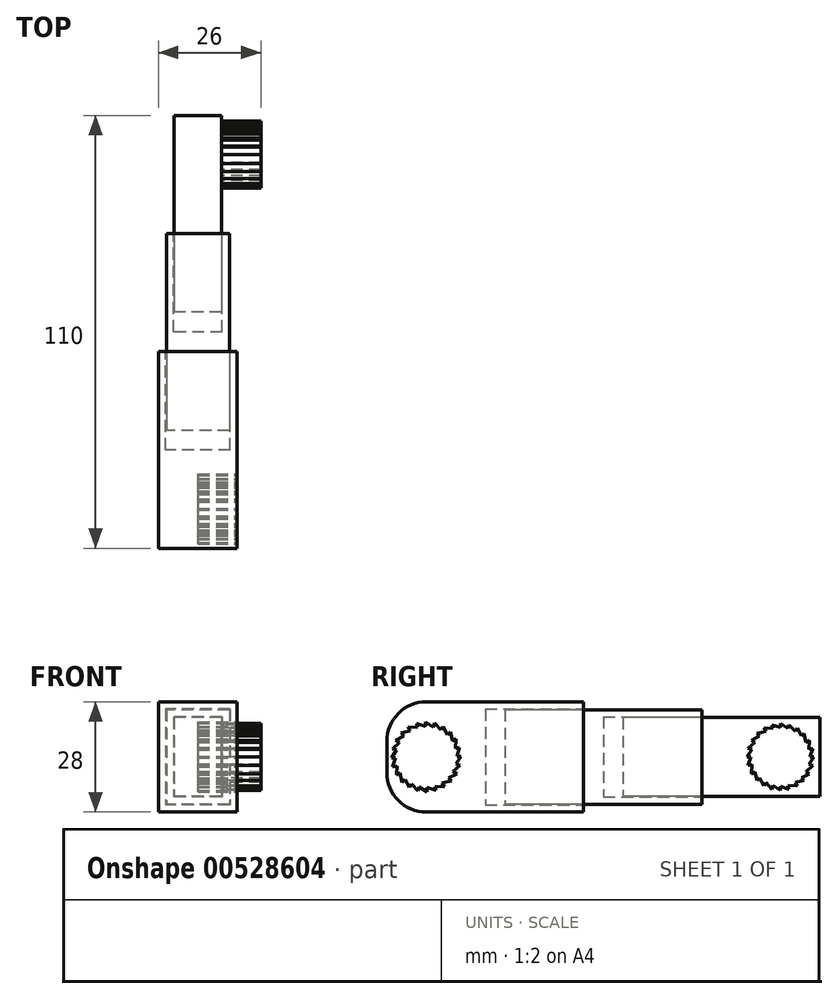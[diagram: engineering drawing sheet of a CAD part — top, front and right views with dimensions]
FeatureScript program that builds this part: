
annotation { "Feature Type Name" : "Feature", "Feature Type Description" : "" }
export const myFeature = defineFeature(function(context is Context, id is Id, definition is map)
    precondition{}
    {
        {
            var Q0;
            Q0=qCreatedBy(makeId("Right.planeOp"),FACE);
            var sketch = newSketch(context, id + "F0", { "sketchPlane" : qUnion([Q0])});
            skLineSegment(sketch, "E0.bottom", {"start": v(50, 0) * mm, "end": v(0, 0) * mm});
            skLineSegment(sketch, "E0.top", {"start": v(50, 28) * mm, "end": v(0, 28) * mm});
            skLineSegment(sketch, "E0.left", {"start": v(50, 0) * mm, "end": v(50, 28) * mm});
            skLineSegment(sketch, "E0.right", {"start": v(0, 0) * mm, "end": v(0, 28) * mm});
            skSolve(sketch);
        }
        {
            var Q0;
            Q0=makeQuery(id+"F0.imprint","IMPRINT",FACE,{"disambiguationData":[TD([[makeQuery(id+"F0.imprint","IMPRINT",EDGE,{"derivedFrom":sQuery(id+"F0.wireOp",EDGE,"E0.bottom")}),-1.0]])]});
            extrude(context, id + "F1", {"entities" : qUnion([Q0]), "depth" : 20 * mm, "offsetDistance" : 25 * mm});
        }
        {
            var Q0;
            Q0=makeQuery(id+"F1.opExtrude","CAP_FACE",FACE,{"disambiguationData":[OSD([sQuery(id+"F0.wireOp",EDGE,"E0.bottom"),sQuery(id+"F0.wireOp",EDGE,"E0.top"),sQuery(id+"F0.wireOp",EDGE,"E0.left"),sQuery(id+"F0.wireOp",EDGE,"E0.right")])],"isStart":false});
            var sketch = newSketch(context, id + "F2", { "sketchPlane" : qUnion([Q0])});
            skCircle(sketch, "E1", {"center": v(10, 14) * mm, "radius": 7.5 * mm});
            skLineSegment(sketch, "E2", {"start": v(10, 21.5) * mm, "end": v(10, 22.5) * mm});
            skPoint(sketch, "E3.center", {"position": v(5.72, 10.17) * mm});
            skLineSegment(sketch, "E4", {"start": v(10, 22.5) * mm, "end": v(11.94, 21.24) * mm});
            skLineSegment(sketch, "E5.1.0", {"start": v(12.2, 22.21) * mm, "end": v(13.75, 20.5) * mm});
            skLineSegment(sketch, "E5.1.1", {"start": v(11.94, 21.24) * mm, "end": v(12.2, 22.21) * mm});
            skLineSegment(sketch, "E5.2.0", {"start": v(14.25, 21.36) * mm, "end": v(15.3, 19.3) * mm});
            skLineSegment(sketch, "E5.2.1", {"start": v(13.75, 20.5) * mm, "end": v(14.25, 21.36) * mm});
            skLineSegment(sketch, "E5.3.0", {"start": v(16.01, 20.01) * mm, "end": v(16.5, 17.75) * mm});
            skLineSegment(sketch, "E5.3.1", {"start": v(15.3, 19.3) * mm, "end": v(16.01, 20.01) * mm});
            skLineSegment(sketch, "E5.4.0", {"start": v(17.36, 18.25) * mm, "end": v(17.24, 15.94) * mm});
            skLineSegment(sketch, "E5.4.1", {"start": v(16.5, 17.75) * mm, "end": v(17.36, 18.25) * mm});
            skLineSegment(sketch, "E5.5.0", {"start": v(18.21, 16.2) * mm, "end": v(17.5, 14) * mm});
            skLineSegment(sketch, "E5.5.1", {"start": v(17.24, 15.94) * mm, "end": v(18.21, 16.2) * mm});
            skLineSegment(sketch, "E5.6.0", {"start": v(18.5, 14) * mm, "end": v(17.24, 12.06) * mm});
            skLineSegment(sketch, "E5.6.1", {"start": v(17.5, 14) * mm, "end": v(18.5, 14) * mm});
            skLineSegment(sketch, "E5.7.0", {"start": v(18.21, 11.8) * mm, "end": v(16.5, 10.25) * mm});
            skLineSegment(sketch, "E5.7.1", {"start": v(17.24, 12.06) * mm, "end": v(18.21, 11.8) * mm});
            skLineSegment(sketch, "E5.8.0", {"start": v(17.36, 9.75) * mm, "end": v(15.3, 8.7) * mm});
            skLineSegment(sketch, "E5.8.1", {"start": v(16.5, 10.25) * mm, "end": v(17.36, 9.75) * mm});
            skLineSegment(sketch, "E5.9.0", {"start": v(16.01, 7.99) * mm, "end": v(13.75, 7.5) * mm});
            skLineSegment(sketch, "E5.9.1", {"start": v(15.3, 8.7) * mm, "end": v(16.01, 7.99) * mm});
            skLineSegment(sketch, "E5.10.0", {"start": v(14.25, 6.64) * mm, "end": v(11.94, 6.76) * mm});
            skLineSegment(sketch, "E5.10.1", {"start": v(13.75, 7.5) * mm, "end": v(14.25, 6.64) * mm});
            skLineSegment(sketch, "E5.11.0", {"start": v(12.2, 5.79) * mm, "end": v(10, 6.5) * mm});
            skLineSegment(sketch, "E5.11.1", {"start": v(11.94, 6.76) * mm, "end": v(12.2, 5.79) * mm});
            skLineSegment(sketch, "E5.12.0", {"start": v(10, 5.5) * mm, "end": v(8.06, 6.76) * mm});
            skLineSegment(sketch, "E5.12.1", {"start": v(10, 6.5) * mm, "end": v(10, 5.5) * mm});
            skLineSegment(sketch, "E5.13.0", {"start": v(7.8, 5.79) * mm, "end": v(6.25, 7.5) * mm});
            skLineSegment(sketch, "E5.13.1", {"start": v(8.06, 6.76) * mm, "end": v(7.8, 5.79) * mm});
            skLineSegment(sketch, "E5.14.0", {"start": v(5.75, 6.64) * mm, "end": v(4.7, 8.7) * mm});
            skLineSegment(sketch, "E5.14.1", {"start": v(6.25, 7.5) * mm, "end": v(5.75, 6.64) * mm});
            skLineSegment(sketch, "E5.15.0", {"start": v(3.99, 7.99) * mm, "end": v(3.5, 10.25) * mm});
            skLineSegment(sketch, "E5.15.1", {"start": v(4.7, 8.7) * mm, "end": v(3.99, 7.99) * mm});
            skLineSegment(sketch, "E5.16.0", {"start": v(2.64, 9.75) * mm, "end": v(2.76, 12.06) * mm});
            skLineSegment(sketch, "E5.16.1", {"start": v(3.5, 10.25) * mm, "end": v(2.64, 9.75) * mm});
            skLineSegment(sketch, "E5.17.0", {"start": v(1.79, 11.8) * mm, "end": v(2.5, 14) * mm});
            skLineSegment(sketch, "E5.17.1", {"start": v(2.76, 12.06) * mm, "end": v(1.79, 11.8) * mm});
            skLineSegment(sketch, "E5.18.0", {"start": v(1.5, 14) * mm, "end": v(2.76, 15.94) * mm});
            skLineSegment(sketch, "E5.18.1", {"start": v(2.5, 14) * mm, "end": v(1.5, 14) * mm});
            skLineSegment(sketch, "E5.19.0", {"start": v(1.79, 16.2) * mm, "end": v(3.5, 17.75) * mm});
            skLineSegment(sketch, "E5.19.1", {"start": v(2.76, 15.94) * mm, "end": v(1.79, 16.2) * mm});
            skLineSegment(sketch, "E5.20.0", {"start": v(2.64, 18.25) * mm, "end": v(4.7, 19.3) * mm});
            skLineSegment(sketch, "E5.20.1", {"start": v(3.5, 17.75) * mm, "end": v(2.64, 18.25) * mm});
            skLineSegment(sketch, "E5.21.0", {"start": v(3.99, 20.01) * mm, "end": v(6.25, 20.5) * mm});
            skLineSegment(sketch, "E5.21.1", {"start": v(4.7, 19.3) * mm, "end": v(3.99, 20.01) * mm});
            skLineSegment(sketch, "E5.22.0", {"start": v(5.75, 21.36) * mm, "end": v(8.06, 21.24) * mm});
            skLineSegment(sketch, "E5.22.1", {"start": v(6.25, 20.5) * mm, "end": v(5.75, 21.36) * mm});
            skLineSegment(sketch, "E5.anchor1", {"start": v(10, 14) * mm, "end": v(10, 21.5) * mm, "construction": true});
            skLineSegment(sketch, "E5.anchor2", {"start": v(10, 14) * mm, "end": v(8.06, 21.24) * mm, "construction": true});
            skLineSegment(sketch, "E6.3.23.0", {"start": v(8.06, 21.24) * mm, "end": v(7.8, 22.21) * mm});
            skLineSegment(sketch, "E6.4.23.0", {"start": v(7.8, 22.21) * mm, "end": v(10, 21.5) * mm});
            skLineSegment(sketch, "E7.0", {"start": v(18.51, 16.49) * mm, "end": v(17.77, 14.2) * mm});
            skLineSegment(sketch, "E7.1", {"start": v(17.46, 16.2) * mm, "end": v(18.51, 16.49) * mm});
            skLineSegment(sketch, "E7.2", {"start": v(2.42, 9.4) * mm, "end": v(2.54, 11.8) * mm});
            skLineSegment(sketch, "E7.3", {"start": v(3.37, 9.94) * mm, "end": v(2.42, 9.4) * mm});
            skLineSegment(sketch, "E7.4", {"start": v(3.87, 7.59) * mm, "end": v(3.37, 9.94) * mm});
            skLineSegment(sketch, "E7.5", {"start": v(4.64, 8.36) * mm, "end": v(3.87, 7.59) * mm});
            skLineSegment(sketch, "E7.6", {"start": v(5.74, 6.22) * mm, "end": v(4.64, 8.36) * mm});
            skLineSegment(sketch, "E7.7", {"start": v(6.29, 7.17) * mm, "end": v(5.74, 6.22) * mm});
            skLineSegment(sketch, "E7.8", {"start": v(7.9, 5.38) * mm, "end": v(6.29, 7.17) * mm});
            skLineSegment(sketch, "E7.9", {"start": v(8.18, 6.44) * mm, "end": v(7.9, 5.38) * mm});
            skLineSegment(sketch, "E7.10", {"start": v(10.2, 5.13) * mm, "end": v(8.18, 6.44) * mm});
            skLineSegment(sketch, "E7.11", {"start": v(10.2, 6.23) * mm, "end": v(10.2, 5.13) * mm});
            skLineSegment(sketch, "E7.12", {"start": v(12.49, 5.49) * mm, "end": v(10.2, 6.23) * mm});
            skLineSegment(sketch, "E7.13", {"start": v(12.2, 6.54) * mm, "end": v(12.49, 5.49) * mm});
            skLineSegment(sketch, "E7.14", {"start": v(18.62, 11.9) * mm, "end": v(16.83, 10.29) * mm});
            skLineSegment(sketch, "E7.15", {"start": v(17.56, 12.18) * mm, "end": v(18.62, 11.9) * mm});
            skLineSegment(sketch, "E7.16", {"start": v(18.87, 14.2) * mm, "end": v(17.56, 12.18) * mm});
            skLineSegment(sketch, "E7.17", {"start": v(17.77, 14.2) * mm, "end": v(18.87, 14.2) * mm});
            skLineSegment(sketch, "E7.18", {"start": v(16.83, 10.29) * mm, "end": v(17.78, 9.74) * mm});
            skLineSegment(sketch, "E7.19", {"start": v(17.78, 9.74) * mm, "end": v(15.64, 8.64) * mm});
            skLineSegment(sketch, "E7.20", {"start": v(15.64, 8.64) * mm, "end": v(16.41, 7.87) * mm});
            skLineSegment(sketch, "E7.21", {"start": v(16.41, 7.87) * mm, "end": v(14.06, 7.37) * mm});
            skLineSegment(sketch, "E7.22", {"start": v(14.06, 7.37) * mm, "end": v(14.6, 6.42) * mm});
            skLineSegment(sketch, "E7.23", {"start": v(14.6, 6.42) * mm, "end": v(12.2, 6.54) * mm});
            skLineSegment(sketch, "E7.24", {"start": v(2.54, 11.8) * mm, "end": v(1.49, 11.51) * mm});
            skLineSegment(sketch, "E7.25", {"start": v(1.49, 11.51) * mm, "end": v(2.23, 13.8) * mm});
            skLineSegment(sketch, "E7.26", {"start": v(2.23, 13.8) * mm, "end": v(1.13, 13.8) * mm});
            skLineSegment(sketch, "E7.27", {"start": v(1.13, 13.8) * mm, "end": v(2.44, 15.82) * mm});
            skLineSegment(sketch, "E7.28", {"start": v(2.44, 15.82) * mm, "end": v(1.38, 16.1) * mm});
            skLineSegment(sketch, "E7.29", {"start": v(1.38, 16.1) * mm, "end": v(3.17, 17.71) * mm});
            skLineSegment(sketch, "E7.30", {"start": v(3.17, 17.71) * mm, "end": v(2.22, 18.26) * mm});
            skLineSegment(sketch, "E7.31", {"start": v(2.22, 18.26) * mm, "end": v(4.36, 19.36) * mm});
            skLineSegment(sketch, "E7.32", {"start": v(4.36, 19.36) * mm, "end": v(3.59, 20.13) * mm});
            skLineSegment(sketch, "E7.33", {"start": v(3.59, 20.13) * mm, "end": v(5.94, 20.63) * mm});
            skLineSegment(sketch, "E7.34", {"start": v(5.94, 20.63) * mm, "end": v(5.4, 21.58) * mm});
            skLineSegment(sketch, "E7.35", {"start": v(5.4, 21.58) * mm, "end": v(7.8, 21.46) * mm});
            skLineSegment(sketch, "E7.36", {"start": v(7.8, 21.46) * mm, "end": v(7.51, 22.51) * mm});
            skLineSegment(sketch, "E7.37", {"start": v(7.51, 22.51) * mm, "end": v(9.8, 21.77) * mm});
            skLineSegment(sketch, "E7.38", {"start": v(9.8, 21.77) * mm, "end": v(9.8, 22.87) * mm});
            skLineSegment(sketch, "E7.39", {"start": v(9.8, 22.87) * mm, "end": v(11.82, 21.56) * mm});
            skLineSegment(sketch, "E7.40", {"start": v(11.82, 21.56) * mm, "end": v(12.1, 22.62) * mm});
            skLineSegment(sketch, "E7.41", {"start": v(12.1, 22.62) * mm, "end": v(13.71, 20.83) * mm});
            skLineSegment(sketch, "E7.42", {"start": v(13.71, 20.83) * mm, "end": v(14.26, 21.78) * mm});
            skLineSegment(sketch, "E7.43", {"start": v(14.26, 21.78) * mm, "end": v(15.36, 19.64) * mm});
            skLineSegment(sketch, "E7.44", {"start": v(15.36, 19.64) * mm, "end": v(16.13, 20.41) * mm});
            skLineSegment(sketch, "E7.45", {"start": v(16.13, 20.41) * mm, "end": v(16.63, 18.06) * mm});
            skLineSegment(sketch, "E7.46", {"start": v(16.63, 18.06) * mm, "end": v(17.58, 18.6) * mm});
            skLineSegment(sketch, "E7.47", {"start": v(17.58, 18.6) * mm, "end": v(17.46, 16.2) * mm});
            skSolve(sketch);
        }
        {
            var Q0;
            {var subQ0=sQuery(id+"F2.wireOp",EDGE,"E1");var subQ17=makeQuery(id+"F2.imprint","INTERSECT",VERTEX,{"derivedFrom":[subQ0,sQuery(id+"F2.wireOp",EDGE,"E5.4.0"),sQuery(id+"F2.wireOp",EDGE,"E5.5.1")]});Q0=makeQuery(id+"F2.imprint","IMPRINT",FACE,{"disambiguationData":[TD([[makeQuery(id+"F2.imprint","IMPRINT",EDGE,{"disambiguationData":[TD([[subQ17,1.0]])],"derivedFrom":subQ0}),1.0]])]});}
            var Q1;
            {var subQ2=sQuery(id+"F2.wireOp",EDGE,"E6.3.23.0");Q1=makeQuery(id+"F2.imprint","IMPRINT",FACE,{"disambiguationData":[TD([[makeQuery(id+"F2.imprint","IMPRINT",EDGE,{"derivedFrom":subQ2}),-1.0]])]});}
            var Q2;
            {var subQ2=sQuery(id+"F2.wireOp",EDGE,"E5.22.0");Q2=makeQuery(id+"F2.imprint","IMPRINT",FACE,{"disambiguationData":[TD([[makeQuery(id+"F2.imprint","IMPRINT",EDGE,{"derivedFrom":subQ2}),-1.0]])]});}
            var Q3;
            {var subQ2=sQuery(id+"F2.wireOp",EDGE,"E5.21.0");Q3=makeQuery(id+"F2.imprint","IMPRINT",FACE,{"disambiguationData":[TD([[makeQuery(id+"F2.imprint","IMPRINT",EDGE,{"derivedFrom":subQ2}),-1.0]])]});}
            var Q4;
            {var subQ2=sQuery(id+"F2.wireOp",EDGE,"E5.20.0");Q4=makeQuery(id+"F2.imprint","IMPRINT",FACE,{"disambiguationData":[TD([[makeQuery(id+"F2.imprint","IMPRINT",EDGE,{"derivedFrom":subQ2}),-1.0]])]});}
            var Q5;
            {var subQ2=sQuery(id+"F2.wireOp",EDGE,"E5.19.0");Q5=makeQuery(id+"F2.imprint","IMPRINT",FACE,{"disambiguationData":[TD([[makeQuery(id+"F2.imprint","IMPRINT",EDGE,{"derivedFrom":subQ2}),-1.0]])]});}
            var Q6;
            {var subQ2=sQuery(id+"F2.wireOp",EDGE,"E5.17.0");Q6=makeQuery(id+"F2.imprint","IMPRINT",FACE,{"disambiguationData":[TD([[makeQuery(id+"F2.imprint","IMPRINT",EDGE,{"derivedFrom":subQ2}),-1.0]])]});}
            var Q7;
            {var subQ2=sQuery(id+"F2.wireOp",EDGE,"E5.18.0");Q7=makeQuery(id+"F2.imprint","IMPRINT",FACE,{"disambiguationData":[TD([[makeQuery(id+"F2.imprint","IMPRINT",EDGE,{"derivedFrom":subQ2}),-1.0]])]});}
            var Q8;
            {var subQ2=sQuery(id+"F2.wireOp",EDGE,"E5.16.0");Q8=makeQuery(id+"F2.imprint","IMPRINT",FACE,{"disambiguationData":[TD([[makeQuery(id+"F2.imprint","IMPRINT",EDGE,{"derivedFrom":subQ2}),-1.0]])]});}
            var Q9;
            {var subQ0=sQuery(id+"F2.wireOp",EDGE,"E2");Q9=makeQuery(id+"F2.imprint","IMPRINT",FACE,{"disambiguationData":[TD([[makeQuery(id+"F2.imprint","IMPRINT",EDGE,{"derivedFrom":subQ0}),-1.0]])]});}
            var Q10;
            {var subQ2=sQuery(id+"F2.wireOp",EDGE,"E5.1.0");Q10=makeQuery(id+"F2.imprint","IMPRINT",FACE,{"disambiguationData":[TD([[makeQuery(id+"F2.imprint","IMPRINT",EDGE,{"derivedFrom":subQ2}),-1.0]])]});}
            var Q11;
            {var subQ2=sQuery(id+"F2.wireOp",EDGE,"E5.2.0");Q11=makeQuery(id+"F2.imprint","IMPRINT",FACE,{"disambiguationData":[TD([[makeQuery(id+"F2.imprint","IMPRINT",EDGE,{"derivedFrom":subQ2}),-1.0]])]});}
            var Q12;
            {var subQ2=sQuery(id+"F2.wireOp",EDGE,"E5.3.0");Q12=makeQuery(id+"F2.imprint","IMPRINT",FACE,{"disambiguationData":[TD([[makeQuery(id+"F2.imprint","IMPRINT",EDGE,{"derivedFrom":subQ2}),-1.0]])]});}
            var Q13;
            {var subQ2=sQuery(id+"F2.wireOp",EDGE,"E5.4.0");Q13=makeQuery(id+"F2.imprint","IMPRINT",FACE,{"disambiguationData":[TD([[makeQuery(id+"F2.imprint","IMPRINT",EDGE,{"derivedFrom":subQ2}),-1.0]])]});}
            var Q14;
            {var subQ2=sQuery(id+"F2.wireOp",EDGE,"E5.5.0");Q14=makeQuery(id+"F2.imprint","IMPRINT",FACE,{"disambiguationData":[TD([[makeQuery(id+"F2.imprint","IMPRINT",EDGE,{"derivedFrom":subQ2}),-1.0]])]});}
            var Q15;
            {var subQ2=sQuery(id+"F2.wireOp",EDGE,"E5.6.0");Q15=makeQuery(id+"F2.imprint","IMPRINT",FACE,{"disambiguationData":[TD([[makeQuery(id+"F2.imprint","IMPRINT",EDGE,{"derivedFrom":subQ2}),-1.0]])]});}
            var Q16;
            {var subQ2=sQuery(id+"F2.wireOp",EDGE,"E5.7.0");Q16=makeQuery(id+"F2.imprint","IMPRINT",FACE,{"disambiguationData":[TD([[makeQuery(id+"F2.imprint","IMPRINT",EDGE,{"derivedFrom":subQ2}),-1.0]])]});}
            var Q17;
            {var subQ2=sQuery(id+"F2.wireOp",EDGE,"E5.8.0");Q17=makeQuery(id+"F2.imprint","IMPRINT",FACE,{"disambiguationData":[TD([[makeQuery(id+"F2.imprint","IMPRINT",EDGE,{"derivedFrom":subQ2}),-1.0]])]});}
            var Q18;
            {var subQ2=sQuery(id+"F2.wireOp",EDGE,"E5.9.0");Q18=makeQuery(id+"F2.imprint","IMPRINT",FACE,{"disambiguationData":[TD([[makeQuery(id+"F2.imprint","IMPRINT",EDGE,{"derivedFrom":subQ2}),-1.0]])]});}
            var Q19;
            {var subQ2=sQuery(id+"F2.wireOp",EDGE,"E5.10.0");Q19=makeQuery(id+"F2.imprint","IMPRINT",FACE,{"disambiguationData":[TD([[makeQuery(id+"F2.imprint","IMPRINT",EDGE,{"derivedFrom":subQ2}),-1.0]])]});}
            var Q20;
            {var subQ2=sQuery(id+"F2.wireOp",EDGE,"E5.11.0");Q20=makeQuery(id+"F2.imprint","IMPRINT",FACE,{"disambiguationData":[TD([[makeQuery(id+"F2.imprint","IMPRINT",EDGE,{"derivedFrom":subQ2}),-1.0]])]});}
            var Q21;
            {var subQ2=sQuery(id+"F2.wireOp",EDGE,"E5.12.0");Q21=makeQuery(id+"F2.imprint","IMPRINT",FACE,{"disambiguationData":[TD([[makeQuery(id+"F2.imprint","IMPRINT",EDGE,{"derivedFrom":subQ2}),-1.0]])]});}
            var Q22;
            {var subQ2=sQuery(id+"F2.wireOp",EDGE,"E5.13.0");Q22=makeQuery(id+"F2.imprint","IMPRINT",FACE,{"disambiguationData":[TD([[makeQuery(id+"F2.imprint","IMPRINT",EDGE,{"derivedFrom":subQ2}),-1.0]])]});}
            var Q23;
            {var subQ2=sQuery(id+"F2.wireOp",EDGE,"E5.14.0");Q23=makeQuery(id+"F2.imprint","IMPRINT",FACE,{"disambiguationData":[TD([[makeQuery(id+"F2.imprint","IMPRINT",EDGE,{"derivedFrom":subQ2}),-1.0]])]});}
            var Q24;
            {var subQ2=sQuery(id+"F2.wireOp",EDGE,"E5.15.0");Q24=makeQuery(id+"F2.imprint","IMPRINT",FACE,{"disambiguationData":[TD([[makeQuery(id+"F2.imprint","IMPRINT",EDGE,{"derivedFrom":subQ2}),-1.0]])]});}
            var Q25;
            Q25=makeQuery(id+"F2.imprint","IMPRINT",FACE,{"disambiguationData":[TD([[makeQuery(id+"F2.imprint","IMPRINT",EDGE,{"derivedFrom":sQuery(id+"F2.wireOp",EDGE,"E2")}),1.0]])]});
            extrude(context, id + "F3", {"entities" : qUnion([Q0, Q1, Q2, Q3, Q4, Q5, Q6, Q7, Q8, Q9, Q10, Q11, Q12, Q13, Q14, Q15, Q16, Q17, Q18, Q19, Q20, Q21, Q22, Q23, Q24, Q25]), "operationType" : NewBodyOperationType.REMOVE, "oppositeDirection" : true, "depth" : 10 * mm, "offsetDistance" : 25 * mm});
        }
        {
            var Q0;
            Q0=makeQuery(id+"F1.opExtrude","SWEPT_EDGE",EDGE,{"disambiguationData":[OSD([sQuery(id+"F0.wireOp",EDGE,"E0.bottom"),sQuery(id+"F0.wireOp",EDGE,"E0.right")])]});
            var Q1;
            Q1=makeQuery(id+"F1.opExtrude","SWEPT_EDGE",EDGE,{"disambiguationData":[OSD([sQuery(id+"F0.wireOp",EDGE,"E0.top"),sQuery(id+"F0.wireOp",EDGE,"E0.right")])]});
            fillet(context, id + "F4", {"entities" : qUnion([Q0, Q1]), "radius" : 10 * mm, "tangentPropagation" : true, "allowEdgeOverflow" : false});
        }
        {
            var Q0;
            Q0=makeQuery(id+"F1.opExtrude","SWEPT_FACE",FACE,{"disambiguationData":[OSD([sQuery(id+"F0.wireOp",EDGE,"E0.left")])]});
            var sketch = newSketch(context, id + "F5", { "sketchPlane" : qUnion([Q0])});
            skLineSegment(sketch, "E8", {"start": v(-20, 28) * mm, "end": v(0, 0) * mm, "construction": true});
            skLineSegment(sketch, "E9", {"start": v(0, 28) * mm, "end": v(-20, 0) * mm, "construction": true});
            skLineSegment(sketch, "E10.bottom", {"start": v(-18, 26) * mm, "end": v(-2, 26) * mm});
            skLineSegment(sketch, "E10.top", {"start": v(-18, 2) * mm, "end": v(-2, 2) * mm});
            skLineSegment(sketch, "E10.left", {"start": v(-18, 26) * mm, "end": v(-18, 2) * mm});
            skLineSegment(sketch, "E10.right", {"start": v(-2, 26) * mm, "end": v(-2, 2) * mm});
            skPoint(sketch, "E10.middle", {"position": v(-10, 14) * mm});
            skLineSegment(sketch, "E11.0", {"start": v(-18.2, 26.2) * mm, "end": v(-1.8, 26.2) * mm});
            skLineSegment(sketch, "E11.1", {"start": v(-18.2, 26.2) * mm, "end": v(-18.2, 1.8) * mm});
            skLineSegment(sketch, "E11.2", {"start": v(-18.2, 1.8) * mm, "end": v(-1.8, 1.8) * mm});
            skLineSegment(sketch, "E11.3", {"start": v(-1.8, 26.2) * mm, "end": v(-1.8, 1.8) * mm});
            skSolve(sketch);
        }
        {
            var Q0;
            Q0=makeQuery(id+"F5.imprint","IMPRINT",FACE,{"disambiguationData":[TD([[makeQuery(id+"F5.imprint","IMPRINT",EDGE,{"derivedFrom":sQuery(id+"F5.wireOp",EDGE,"E10.bottom")}),-1.0]])]});
            var Q1;
            Q1=makeQuery(id+"F5.imprint","IMPRINT",FACE,{"disambiguationData":[TD([[makeQuery(id+"F5.imprint","IMPRINT",EDGE,{"derivedFrom":sQuery(id+"F5.wireOp",EDGE,"E10.bottom")}),1.0]])]});
            extrude(context, id + "F6", {"entities" : qUnion([Q0, Q1]), "operationType" : NewBodyOperationType.REMOVE, "oppositeDirection" : true, "depth" : 25 * mm, "offsetDistance" : 25 * mm});
        }
        {
            var Q0;
            Q0=makeQuery(id+"F5.imprint","IMPRINT",FACE,{"disambiguationData":[TD([[makeQuery(id+"F5.imprint","IMPRINT",EDGE,{"derivedFrom":sQuery(id+"F5.wireOp",EDGE,"E10.bottom")}),-1.0]])]});
            extrude(context, id + "F7", {"entities" : qUnion([Q0]), "depth" : 30 * mm, "offsetDistance" : 25 * mm, "hasSecondDirection" : true, "secondDirectionOppositeDirection" : true, "secondDirectionDepth" : 20 * mm});
        }
        {
            var Q0;
            Q0=makeQuery(id+"F7.opExtrude","CAP_FACE",FACE,{"disambiguationData":[OSD([sQuery(id+"F5.wireOp",EDGE,"E10.bottom"),sQuery(id+"F5.wireOp",EDGE,"E10.top"),sQuery(id+"F5.wireOp",EDGE,"E10.left"),sQuery(id+"F5.wireOp",EDGE,"E10.right")])],"isStart":false});
            var sketch = newSketch(context, id + "F8", { "sketchPlane" : qUnion([Q0])});
            skLineSegment(sketch, "E12", {"start": v(-18, 2) * mm, "end": v(-2, 26) * mm, "construction": true});
            skLineSegment(sketch, "E13", {"start": v(-18, 26) * mm, "end": v(-2, 2) * mm, "construction": true});
            skLineSegment(sketch, "E14.bottom", {"start": v(-16, 24) * mm, "end": v(-4, 24) * mm});
            skLineSegment(sketch, "E14.top", {"start": v(-16, 4) * mm, "end": v(-4, 4) * mm});
            skLineSegment(sketch, "E14.left", {"start": v(-16, 24) * mm, "end": v(-16, 4) * mm});
            skLineSegment(sketch, "E14.right", {"start": v(-4, 24) * mm, "end": v(-4, 4) * mm});
            skPoint(sketch, "E14.middle", {"position": v(-10, 14) * mm});
            skLineSegment(sketch, "E15.0", {"start": v(-16.2, 24.2) * mm, "end": v(-16.2, 3.8) * mm});
            skLineSegment(sketch, "E15.1", {"start": v(-16.2, 24.2) * mm, "end": v(-3.8, 24.2) * mm});
            skLineSegment(sketch, "E15.2", {"start": v(-3.8, 24.2) * mm, "end": v(-3.8, 3.8) * mm});
            skLineSegment(sketch, "E15.3", {"start": v(-16.2, 3.8) * mm, "end": v(-3.8, 3.8) * mm});
            skSolve(sketch);
        }
        {
            var Q0;
            Q0=makeQuery(id+"F8.imprint","IMPRINT",FACE,{"disambiguationData":[TD([[makeQuery(id+"F8.imprint","IMPRINT",EDGE,{"derivedFrom":sQuery(id+"F8.wireOp",EDGE,"E14.bottom")}),1.0]])]});
            var Q1;
            Q1=makeQuery(id+"F8.imprint","IMPRINT",FACE,{"disambiguationData":[TD([[makeQuery(id+"F8.imprint","IMPRINT",EDGE,{"derivedFrom":sQuery(id+"F8.wireOp",EDGE,"E14.bottom")}),-1.0]])]});
            extrude(context, id + "F9", {"entities" : qUnion([Q0, Q1]), "operationType" : NewBodyOperationType.REMOVE, "oppositeDirection" : true, "depth" : 25 * mm, "offsetDistance" : 25 * mm});
        }
        {
            var Q0;
            Q0=makeQuery(id+"F8.imprint","IMPRINT",FACE,{"disambiguationData":[TD([[makeQuery(id+"F8.imprint","IMPRINT",EDGE,{"derivedFrom":sQuery(id+"F8.wireOp",EDGE,"E14.bottom")}),-1.0]])]});
            extrude(context, id + "F10", {"entities" : qUnion([Q0]), "depth" : 30 * mm, "offsetDistance" : 25 * mm, "hasSecondDirection" : true, "secondDirectionOppositeDirection" : true, "secondDirectionDepth" : 20 * mm});
        }
        {
            var Q0;
            Q0=makeQuery(id+"F10.opExtrude","SWEPT_FACE",FACE,{"disambiguationData":[OSD([sQuery(id+"F8.wireOp",EDGE,"E14.left")])]});
            var sketch = newSketch(context, id + "F11", { "sketchPlane" : qUnion([Q0])});
            skCircle(sketch, "E16", {"center": v(100, 14) * mm, "radius": 7.5 * mm});
            skLineSegment(sketch, "E17", {"start": v(100, 21.5) * mm, "end": v(100, 22.5) * mm});
            skPoint(sketch, "E18.center", {"position": v(83.72, 12) * mm});
            skLineSegment(sketch, "E19", {"start": v(100, 22.5) * mm, "end": v(101.94, 21.24) * mm});
            skLineSegment(sketch, "E20.1.0", {"start": v(102.2, 22.21) * mm, "end": v(103.75, 20.5) * mm});
            skLineSegment(sketch, "E20.1.1", {"start": v(101.94, 21.24) * mm, "end": v(102.2, 22.21) * mm});
            skLineSegment(sketch, "E20.2.0", {"start": v(104.25, 21.36) * mm, "end": v(105.3, 19.3) * mm});
            skLineSegment(sketch, "E20.2.1", {"start": v(103.75, 20.5) * mm, "end": v(104.25, 21.36) * mm});
            skLineSegment(sketch, "E20.3.0", {"start": v(106.01, 20.01) * mm, "end": v(106.5, 17.75) * mm});
            skLineSegment(sketch, "E20.3.1", {"start": v(105.3, 19.3) * mm, "end": v(106.01, 20.01) * mm});
            skLineSegment(sketch, "E20.4.0", {"start": v(107.36, 18.25) * mm, "end": v(107.24, 15.94) * mm});
            skLineSegment(sketch, "E20.4.1", {"start": v(106.5, 17.75) * mm, "end": v(107.36, 18.25) * mm});
            skLineSegment(sketch, "E20.5.0", {"start": v(108.21, 16.2) * mm, "end": v(107.5, 14) * mm});
            skLineSegment(sketch, "E20.5.1", {"start": v(107.24, 15.94) * mm, "end": v(108.21, 16.2) * mm});
            skLineSegment(sketch, "E20.6.0", {"start": v(108.5, 14) * mm, "end": v(107.24, 12.06) * mm});
            skLineSegment(sketch, "E20.6.1", {"start": v(107.5, 14) * mm, "end": v(108.5, 14) * mm});
            skLineSegment(sketch, "E20.7.0", {"start": v(108.21, 11.8) * mm, "end": v(106.5, 10.25) * mm});
            skLineSegment(sketch, "E20.7.1", {"start": v(107.24, 12.06) * mm, "end": v(108.21, 11.8) * mm});
            skLineSegment(sketch, "E20.8.0", {"start": v(107.36, 9.75) * mm, "end": v(105.3, 8.7) * mm});
            skLineSegment(sketch, "E20.8.1", {"start": v(106.5, 10.25) * mm, "end": v(107.36, 9.75) * mm});
            skLineSegment(sketch, "E20.9.0", {"start": v(106.01, 7.99) * mm, "end": v(103.75, 7.5) * mm});
            skLineSegment(sketch, "E20.9.1", {"start": v(105.3, 8.7) * mm, "end": v(106.01, 7.99) * mm});
            skLineSegment(sketch, "E20.10.0", {"start": v(104.25, 6.64) * mm, "end": v(101.94, 6.76) * mm});
            skLineSegment(sketch, "E20.10.1", {"start": v(103.75, 7.5) * mm, "end": v(104.25, 6.64) * mm});
            skLineSegment(sketch, "E20.11.0", {"start": v(102.2, 5.79) * mm, "end": v(100, 6.5) * mm});
            skLineSegment(sketch, "E20.11.1", {"start": v(101.94, 6.76) * mm, "end": v(102.2, 5.79) * mm});
            skLineSegment(sketch, "E20.12.0", {"start": v(100, 5.5) * mm, "end": v(98.06, 6.76) * mm});
            skLineSegment(sketch, "E20.12.1", {"start": v(100, 6.5) * mm, "end": v(100, 5.5) * mm});
            skLineSegment(sketch, "E20.13.0", {"start": v(97.8, 5.79) * mm, "end": v(96.25, 7.5) * mm});
            skLineSegment(sketch, "E20.13.1", {"start": v(98.06, 6.76) * mm, "end": v(97.8, 5.79) * mm});
            skLineSegment(sketch, "E20.14.0", {"start": v(95.75, 6.64) * mm, "end": v(94.7, 8.7) * mm});
            skLineSegment(sketch, "E20.14.1", {"start": v(96.25, 7.5) * mm, "end": v(95.75, 6.64) * mm});
            skLineSegment(sketch, "E20.15.0", {"start": v(93.99, 7.99) * mm, "end": v(93.5, 10.25) * mm});
            skLineSegment(sketch, "E20.15.1", {"start": v(94.7, 8.7) * mm, "end": v(93.99, 7.99) * mm});
            skLineSegment(sketch, "E20.16.0", {"start": v(92.64, 9.75) * mm, "end": v(92.76, 12.06) * mm});
            skLineSegment(sketch, "E20.16.1", {"start": v(93.5, 10.25) * mm, "end": v(92.64, 9.75) * mm});
            skLineSegment(sketch, "E20.17.0", {"start": v(91.79, 11.8) * mm, "end": v(92.5, 14) * mm});
            skLineSegment(sketch, "E20.17.1", {"start": v(92.76, 12.06) * mm, "end": v(91.79, 11.8) * mm});
            skLineSegment(sketch, "E20.18.0", {"start": v(91.5, 14) * mm, "end": v(92.76, 15.94) * mm});
            skLineSegment(sketch, "E20.18.1", {"start": v(92.5, 14) * mm, "end": v(91.5, 14) * mm});
            skLineSegment(sketch, "E20.19.0", {"start": v(91.79, 16.2) * mm, "end": v(93.5, 17.75) * mm});
            skLineSegment(sketch, "E20.19.1", {"start": v(92.76, 15.94) * mm, "end": v(91.79, 16.2) * mm});
            skLineSegment(sketch, "E20.20.0", {"start": v(92.64, 18.25) * mm, "end": v(94.7, 19.3) * mm});
            skLineSegment(sketch, "E20.20.1", {"start": v(93.5, 17.75) * mm, "end": v(92.64, 18.25) * mm});
            skLineSegment(sketch, "E20.21.0", {"start": v(93.99, 20.01) * mm, "end": v(96.25, 20.5) * mm});
            skLineSegment(sketch, "E20.21.1", {"start": v(94.7, 19.3) * mm, "end": v(93.99, 20.01) * mm});
            skLineSegment(sketch, "E20.22.0", {"start": v(95.75, 21.36) * mm, "end": v(98.06, 21.24) * mm});
            skLineSegment(sketch, "E20.22.1", {"start": v(96.25, 20.5) * mm, "end": v(95.75, 21.36) * mm});
            skLineSegment(sketch, "E20.anchor1", {"start": v(100, 14) * mm, "end": v(100, 21.5) * mm, "construction": true});
            skLineSegment(sketch, "E20.anchor2", {"start": v(100, 14) * mm, "end": v(98.06, 21.24) * mm, "construction": true});
            skLineSegment(sketch, "E21.3.23.0", {"start": v(98.06, 21.24) * mm, "end": v(97.8, 22.21) * mm});
            skLineSegment(sketch, "E21.4.23.0", {"start": v(97.8, 22.21) * mm, "end": v(100, 21.5) * mm});
            skLineSegment(sketch, "E22.0", {"start": v(108.51, 16.49) * mm, "end": v(107.77, 14.2) * mm});
            skLineSegment(sketch, "E22.1", {"start": v(107.46, 16.2) * mm, "end": v(108.51, 16.49) * mm});
            skLineSegment(sketch, "E22.2", {"start": v(92.42, 9.4) * mm, "end": v(92.54, 11.8) * mm});
            skLineSegment(sketch, "E22.3", {"start": v(93.37, 9.94) * mm, "end": v(92.42, 9.4) * mm});
            skLineSegment(sketch, "E22.4", {"start": v(93.87, 7.59) * mm, "end": v(93.37, 9.94) * mm});
            skLineSegment(sketch, "E22.5", {"start": v(94.64, 8.36) * mm, "end": v(93.87, 7.59) * mm});
            skLineSegment(sketch, "E22.6", {"start": v(95.74, 6.22) * mm, "end": v(94.64, 8.36) * mm});
            skLineSegment(sketch, "E22.7", {"start": v(96.29, 7.17) * mm, "end": v(95.74, 6.22) * mm});
            skLineSegment(sketch, "E22.8", {"start": v(97.9, 5.38) * mm, "end": v(96.29, 7.17) * mm});
            skLineSegment(sketch, "E22.9", {"start": v(98.18, 6.44) * mm, "end": v(97.9, 5.38) * mm});
            skLineSegment(sketch, "E22.10", {"start": v(100.2, 5.13) * mm, "end": v(98.18, 6.44) * mm});
            skLineSegment(sketch, "E22.11", {"start": v(100.2, 6.23) * mm, "end": v(100.2, 5.13) * mm});
            skLineSegment(sketch, "E22.12", {"start": v(102.49, 5.49) * mm, "end": v(100.2, 6.23) * mm});
            skLineSegment(sketch, "E22.13", {"start": v(102.2, 6.54) * mm, "end": v(102.49, 5.49) * mm});
            skLineSegment(sketch, "E22.14", {"start": v(108.62, 11.9) * mm, "end": v(106.83, 10.29) * mm});
            skLineSegment(sketch, "E22.15", {"start": v(107.56, 12.18) * mm, "end": v(108.62, 11.9) * mm});
            skLineSegment(sketch, "E22.16", {"start": v(108.87, 14.2) * mm, "end": v(107.56, 12.18) * mm});
            skLineSegment(sketch, "E22.17", {"start": v(107.77, 14.2) * mm, "end": v(108.87, 14.2) * mm});
            skLineSegment(sketch, "E22.18", {"start": v(106.83, 10.29) * mm, "end": v(107.78, 9.74) * mm});
            skLineSegment(sketch, "E22.19", {"start": v(107.78, 9.74) * mm, "end": v(105.64, 8.64) * mm});
            skLineSegment(sketch, "E22.20", {"start": v(105.64, 8.64) * mm, "end": v(106.41, 7.87) * mm});
            skLineSegment(sketch, "E22.21", {"start": v(106.41, 7.87) * mm, "end": v(104.06, 7.37) * mm});
            skLineSegment(sketch, "E22.22", {"start": v(104.06, 7.37) * mm, "end": v(104.6, 6.42) * mm});
            skLineSegment(sketch, "E22.23", {"start": v(104.6, 6.42) * mm, "end": v(102.2, 6.54) * mm});
            skLineSegment(sketch, "E22.24", {"start": v(92.54, 11.8) * mm, "end": v(91.49, 11.51) * mm});
            skLineSegment(sketch, "E22.25", {"start": v(91.49, 11.51) * mm, "end": v(92.23, 13.8) * mm});
            skLineSegment(sketch, "E22.26", {"start": v(92.23, 13.8) * mm, "end": v(91.13, 13.8) * mm});
            skLineSegment(sketch, "E22.27", {"start": v(91.13, 13.8) * mm, "end": v(92.44, 15.82) * mm});
            skLineSegment(sketch, "E22.28", {"start": v(92.44, 15.82) * mm, "end": v(91.38, 16.1) * mm});
            skLineSegment(sketch, "E22.29", {"start": v(91.38, 16.1) * mm, "end": v(93.17, 17.71) * mm});
            skLineSegment(sketch, "E22.30", {"start": v(93.17, 17.71) * mm, "end": v(92.22, 18.26) * mm});
            skLineSegment(sketch, "E22.31", {"start": v(92.22, 18.26) * mm, "end": v(94.36, 19.36) * mm});
            skLineSegment(sketch, "E22.32", {"start": v(94.36, 19.36) * mm, "end": v(93.59, 20.13) * mm});
            skLineSegment(sketch, "E22.33", {"start": v(93.59, 20.13) * mm, "end": v(95.94, 20.63) * mm});
            skLineSegment(sketch, "E22.34", {"start": v(95.94, 20.63) * mm, "end": v(95.4, 21.58) * mm});
            skLineSegment(sketch, "E22.35", {"start": v(95.4, 21.58) * mm, "end": v(97.8, 21.46) * mm});
            skLineSegment(sketch, "E22.36", {"start": v(97.8, 21.46) * mm, "end": v(97.51, 22.51) * mm});
            skLineSegment(sketch, "E22.37", {"start": v(97.51, 22.51) * mm, "end": v(99.8, 21.77) * mm});
            skLineSegment(sketch, "E22.38", {"start": v(99.8, 21.77) * mm, "end": v(99.8, 22.87) * mm});
            skLineSegment(sketch, "E22.39", {"start": v(99.8, 22.87) * mm, "end": v(101.82, 21.56) * mm});
            skLineSegment(sketch, "E22.40", {"start": v(101.82, 21.56) * mm, "end": v(102.1, 22.62) * mm});
            skLineSegment(sketch, "E22.41", {"start": v(102.1, 22.62) * mm, "end": v(103.71, 20.83) * mm});
            skLineSegment(sketch, "E22.42", {"start": v(103.71, 20.83) * mm, "end": v(104.26, 21.78) * mm});
            skLineSegment(sketch, "E22.43", {"start": v(104.26, 21.78) * mm, "end": v(105.36, 19.64) * mm});
            skLineSegment(sketch, "E22.44", {"start": v(105.36, 19.64) * mm, "end": v(106.13, 20.41) * mm});
            skLineSegment(sketch, "E22.45", {"start": v(106.13, 20.41) * mm, "end": v(106.63, 18.06) * mm});
            skLineSegment(sketch, "E22.46", {"start": v(106.63, 18.06) * mm, "end": v(107.58, 18.6) * mm});
            skLineSegment(sketch, "E22.47", {"start": v(107.58, 18.6) * mm, "end": v(107.46, 16.2) * mm});
            skSolve(sketch);
        }
        {
            var Q0;
            {var subQ0=sQuery(id+"F11.wireOp",EDGE,"E16");var subQ17=makeQuery(id+"F11.imprint","INTERSECT",VERTEX,{"derivedFrom":[subQ0,sQuery(id+"F11.wireOp",EDGE,"E20.4.0"),sQuery(id+"F11.wireOp",EDGE,"E20.5.1")]});Q0=makeQuery(id+"F11.imprint","IMPRINT",FACE,{"disambiguationData":[TD([[makeQuery(id+"F11.imprint","IMPRINT",EDGE,{"disambiguationData":[TD([[subQ17,1.0]])],"derivedFrom":subQ0}),1.0]])]});}
            var Q1;
            {var subQ2=sQuery(id+"F11.wireOp",EDGE,"E20.7.0");Q1=makeQuery(id+"F11.imprint","IMPRINT",FACE,{"disambiguationData":[TD([[makeQuery(id+"F11.imprint","IMPRINT",EDGE,{"derivedFrom":subQ2}),-1.0]])]});}
            var Q2;
            {var subQ2=sQuery(id+"F11.wireOp",EDGE,"E20.6.0");Q2=makeQuery(id+"F11.imprint","IMPRINT",FACE,{"disambiguationData":[TD([[makeQuery(id+"F11.imprint","IMPRINT",EDGE,{"derivedFrom":subQ2}),-1.0]])]});}
            var Q3;
            {var subQ2=sQuery(id+"F11.wireOp",EDGE,"E20.5.0");Q3=makeQuery(id+"F11.imprint","IMPRINT",FACE,{"disambiguationData":[TD([[makeQuery(id+"F11.imprint","IMPRINT",EDGE,{"derivedFrom":subQ2}),-1.0]])]});}
            var Q4;
            {var subQ2=sQuery(id+"F11.wireOp",EDGE,"E20.4.0");Q4=makeQuery(id+"F11.imprint","IMPRINT",FACE,{"disambiguationData":[TD([[makeQuery(id+"F11.imprint","IMPRINT",EDGE,{"derivedFrom":subQ2}),-1.0]])]});}
            var Q5;
            {var subQ2=sQuery(id+"F11.wireOp",EDGE,"E20.3.0");Q5=makeQuery(id+"F11.imprint","IMPRINT",FACE,{"disambiguationData":[TD([[makeQuery(id+"F11.imprint","IMPRINT",EDGE,{"derivedFrom":subQ2}),-1.0]])]});}
            var Q6;
            {var subQ2=sQuery(id+"F11.wireOp",EDGE,"E20.2.0");Q6=makeQuery(id+"F11.imprint","IMPRINT",FACE,{"disambiguationData":[TD([[makeQuery(id+"F11.imprint","IMPRINT",EDGE,{"derivedFrom":subQ2}),-1.0]])]});}
            var Q7;
            {var subQ2=sQuery(id+"F11.wireOp",EDGE,"E20.1.0");Q7=makeQuery(id+"F11.imprint","IMPRINT",FACE,{"disambiguationData":[TD([[makeQuery(id+"F11.imprint","IMPRINT",EDGE,{"derivedFrom":subQ2}),-1.0]])]});}
            var Q8;
            {var subQ0=sQuery(id+"F11.wireOp",EDGE,"E17");Q8=makeQuery(id+"F11.imprint","IMPRINT",FACE,{"disambiguationData":[TD([[makeQuery(id+"F11.imprint","IMPRINT",EDGE,{"derivedFrom":subQ0}),-1.0]])]});}
            var Q9;
            {var subQ2=sQuery(id+"F11.wireOp",EDGE,"E21.3.23.0");Q9=makeQuery(id+"F11.imprint","IMPRINT",FACE,{"disambiguationData":[TD([[makeQuery(id+"F11.imprint","IMPRINT",EDGE,{"derivedFrom":subQ2}),-1.0]])]});}
            var Q10;
            {var subQ2=sQuery(id+"F11.wireOp",EDGE,"E20.22.0");Q10=makeQuery(id+"F11.imprint","IMPRINT",FACE,{"disambiguationData":[TD([[makeQuery(id+"F11.imprint","IMPRINT",EDGE,{"derivedFrom":subQ2}),-1.0]])]});}
            var Q11;
            {var subQ2=sQuery(id+"F11.wireOp",EDGE,"E20.21.0");Q11=makeQuery(id+"F11.imprint","IMPRINT",FACE,{"disambiguationData":[TD([[makeQuery(id+"F11.imprint","IMPRINT",EDGE,{"derivedFrom":subQ2}),-1.0]])]});}
            var Q12;
            {var subQ2=sQuery(id+"F11.wireOp",EDGE,"E20.20.0");Q12=makeQuery(id+"F11.imprint","IMPRINT",FACE,{"disambiguationData":[TD([[makeQuery(id+"F11.imprint","IMPRINT",EDGE,{"derivedFrom":subQ2}),-1.0]])]});}
            var Q13;
            {var subQ2=sQuery(id+"F11.wireOp",EDGE,"E20.19.0");Q13=makeQuery(id+"F11.imprint","IMPRINT",FACE,{"disambiguationData":[TD([[makeQuery(id+"F11.imprint","IMPRINT",EDGE,{"derivedFrom":subQ2}),-1.0]])]});}
            var Q14;
            {var subQ2=sQuery(id+"F11.wireOp",EDGE,"E20.18.0");Q14=makeQuery(id+"F11.imprint","IMPRINT",FACE,{"disambiguationData":[TD([[makeQuery(id+"F11.imprint","IMPRINT",EDGE,{"derivedFrom":subQ2}),-1.0]])]});}
            var Q15;
            {var subQ2=sQuery(id+"F11.wireOp",EDGE,"E20.17.0");Q15=makeQuery(id+"F11.imprint","IMPRINT",FACE,{"disambiguationData":[TD([[makeQuery(id+"F11.imprint","IMPRINT",EDGE,{"derivedFrom":subQ2}),-1.0]])]});}
            var Q16;
            {var subQ2=sQuery(id+"F11.wireOp",EDGE,"E20.16.0");Q16=makeQuery(id+"F11.imprint","IMPRINT",FACE,{"disambiguationData":[TD([[makeQuery(id+"F11.imprint","IMPRINT",EDGE,{"derivedFrom":subQ2}),-1.0]])]});}
            var Q17;
            {var subQ2=sQuery(id+"F11.wireOp",EDGE,"E20.15.0");Q17=makeQuery(id+"F11.imprint","IMPRINT",FACE,{"disambiguationData":[TD([[makeQuery(id+"F11.imprint","IMPRINT",EDGE,{"derivedFrom":subQ2}),-1.0]])]});}
            var Q18;
            {var subQ2=sQuery(id+"F11.wireOp",EDGE,"E20.14.0");Q18=makeQuery(id+"F11.imprint","IMPRINT",FACE,{"disambiguationData":[TD([[makeQuery(id+"F11.imprint","IMPRINT",EDGE,{"derivedFrom":subQ2}),-1.0]])]});}
            var Q19;
            {var subQ2=sQuery(id+"F11.wireOp",EDGE,"E20.13.0");Q19=makeQuery(id+"F11.imprint","IMPRINT",FACE,{"disambiguationData":[TD([[makeQuery(id+"F11.imprint","IMPRINT",EDGE,{"derivedFrom":subQ2}),-1.0]])]});}
            var Q20;
            {var subQ2=sQuery(id+"F11.wireOp",EDGE,"E20.12.0");Q20=makeQuery(id+"F11.imprint","IMPRINT",FACE,{"disambiguationData":[TD([[makeQuery(id+"F11.imprint","IMPRINT",EDGE,{"derivedFrom":subQ2}),-1.0]])]});}
            var Q21;
            {var subQ2=sQuery(id+"F11.wireOp",EDGE,"E20.8.0");Q21=makeQuery(id+"F11.imprint","IMPRINT",FACE,{"disambiguationData":[TD([[makeQuery(id+"F11.imprint","IMPRINT",EDGE,{"derivedFrom":subQ2}),-1.0]])]});}
            var Q22;
            {var subQ2=sQuery(id+"F11.wireOp",EDGE,"E20.9.0");Q22=makeQuery(id+"F11.imprint","IMPRINT",FACE,{"disambiguationData":[TD([[makeQuery(id+"F11.imprint","IMPRINT",EDGE,{"derivedFrom":subQ2}),-1.0]])]});}
            var Q23;
            {var subQ2=sQuery(id+"F11.wireOp",EDGE,"E20.10.0");Q23=makeQuery(id+"F11.imprint","IMPRINT",FACE,{"disambiguationData":[TD([[makeQuery(id+"F11.imprint","IMPRINT",EDGE,{"derivedFrom":subQ2}),-1.0]])]});}
            var Q24;
            {var subQ2=sQuery(id+"F11.wireOp",EDGE,"E20.11.0");Q24=makeQuery(id+"F11.imprint","IMPRINT",FACE,{"disambiguationData":[TD([[makeQuery(id+"F11.imprint","IMPRINT",EDGE,{"derivedFrom":subQ2}),-1.0]])]});}
            extrude(context, id + "F12", {"entities" : qUnion([Q0, Q1, Q2, Q3, Q4, Q5, Q6, Q7, Q8, Q9, Q10, Q11, Q12, Q13, Q14, Q15, Q16, Q17, Q18, Q19, Q20, Q21, Q22, Q23, Q24]), "operationType" : NewBodyOperationType.ADD, "depth" : 10 * mm, "offsetDistance" : 25 * mm});
        }
    });
